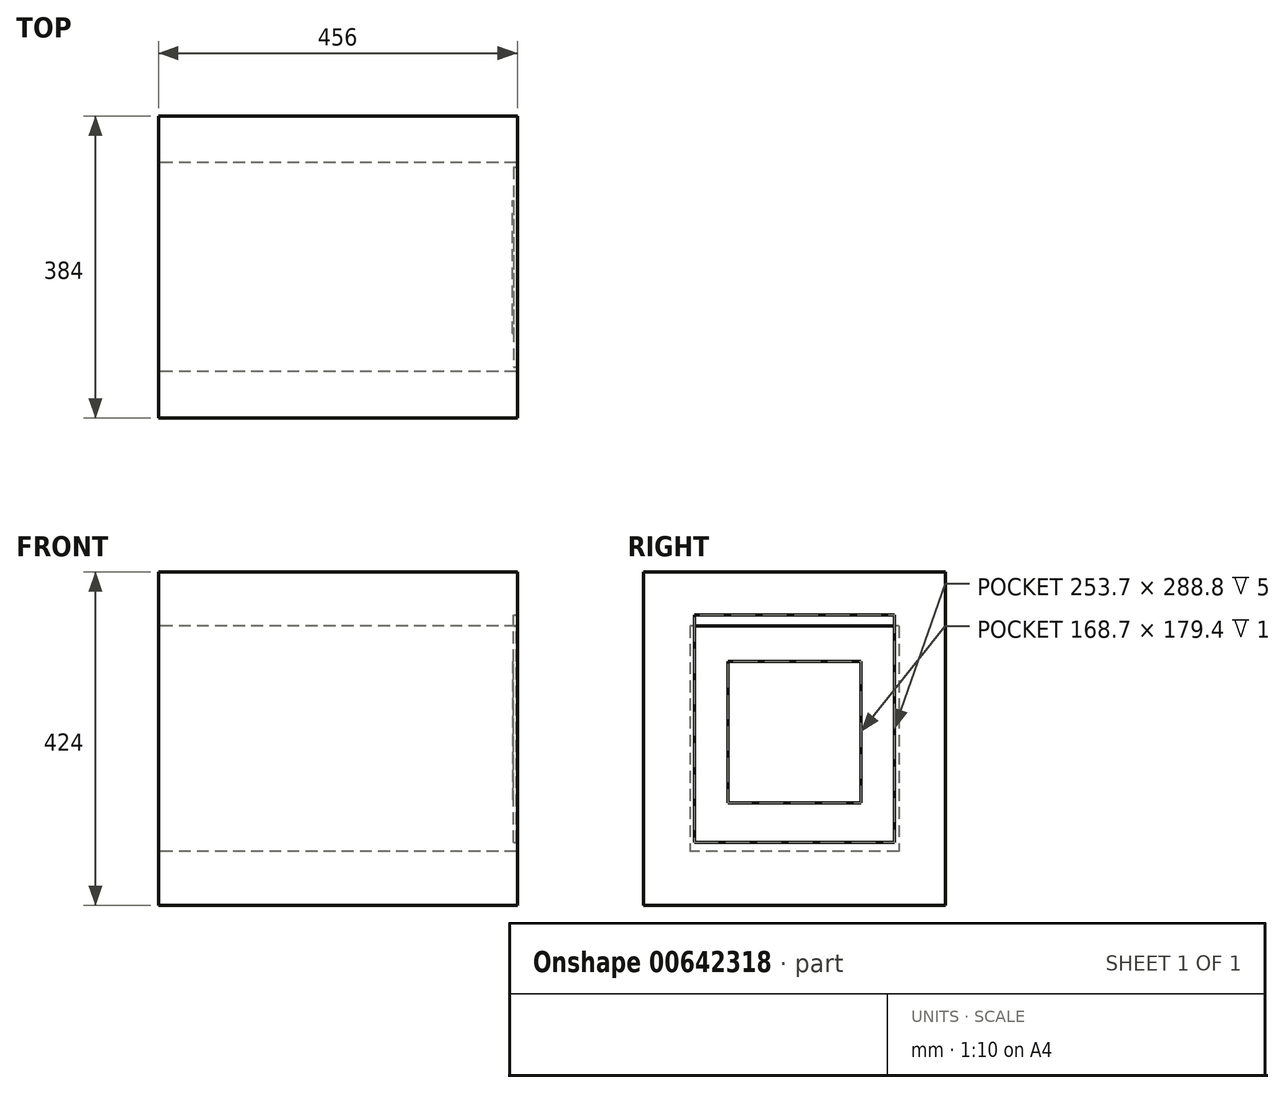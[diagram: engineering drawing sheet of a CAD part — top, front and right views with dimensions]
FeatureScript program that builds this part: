
annotation { "Feature Type Name" : "Feature", "Feature Type Description" : "" }
export const myFeature = defineFeature(function(context is Context, id is Id, definition is map)
    precondition{}
    {
        {
            var Q0;
            Q0=qCreatedBy(makeId("Right.planeOp"),FACE);
            var sketch = newSketch(context, id + "F0", { "sketchPlane" : qUnion([Q0])});
            skLineSegment(sketch, "E0.bottom", {"start": v(132.5, 143) * mm, "end": v(-132.5, 143) * mm});
            skLineSegment(sketch, "E0.top", {"start": v(132.5, -143) * mm, "end": v(-132.5, -143) * mm});
            skLineSegment(sketch, "E0.left", {"start": v(132.5, 143) * mm, "end": v(132.5, -143) * mm});
            skLineSegment(sketch, "E0.right", {"start": v(-132.5, 143) * mm, "end": v(-132.5, -143) * mm});
            skPoint(sketch, "E0.middle", {"position": v(0, 0) * mm});
            skSolve(sketch);
        }
        {
            var Q0;
            Q0=makeQuery(id+"F0.imprint","IMPRINT",FACE,{"disambiguationData":[TD([[makeQuery(id+"F0.imprint","IMPRINT",EDGE,{"derivedFrom":sQuery(id+"F0.wireOp",EDGE,"E0.bottom")}),1.0]])]});
            extrude(context, id + "F1", {"entities" : qUnion([Q0]), "depth" : 455 * mm, "offsetDistance" : 25 * mm});
        }
        {
            var Q0;
            Q0=makeQuery(id+"F1.opExtrude","CAP_FACE",FACE,{"disambiguationData":[OSD([sQuery(id+"F0.wireOp",EDGE,"E0.bottom"),sQuery(id+"F0.wireOp",EDGE,"E0.top"),sQuery(id+"F0.wireOp",EDGE,"E0.left"),sQuery(id+"F0.wireOp",EDGE,"E0.right")])],"isStart":false});
            var sketch = newSketch(context, id + "F2", { "sketchPlane" : qUnion([Q0])});
            skLineSegment(sketch, "E1.bottom", {"start": v(-84.35, 98) * mm, "end": v(84.35, 98) * mm});
            skLineSegment(sketch, "E1.top", {"start": v(-84.35, -81.4) * mm, "end": v(84.35, -81.4) * mm});
            skLineSegment(sketch, "E1.left", {"start": v(-84.35, 98) * mm, "end": v(-84.35, -81.4) * mm});
            skLineSegment(sketch, "E1.right", {"start": v(84.35, 98) * mm, "end": v(84.35, -81.4) * mm});
            skLineSegment(sketch, "E2", {"start": v(-84.35, 98) * mm, "end": v(-132.5, 98) * mm, "construction": true});
            skLineSegment(sketch, "E3", {"start": v(84.35, 98) * mm, "end": v(132.5, 98) * mm, "construction": true});
            skSolve(sketch);
        }
        {
            var Q0;
            Q0=makeQuery(id+"F2.imprint","IMPRINT",FACE,{"disambiguationData":[TD([[makeQuery(id+"F2.imprint","IMPRINT",EDGE,{"derivedFrom":sQuery(id+"F2.wireOp",EDGE,"E1.bottom")}),-1.0]])]});
            extrude(context, id + "F3", {"entities" : qUnion([Q0]), "operationType" : NewBodyOperationType.REMOVE, "oppositeDirection" : true, "depth" : 5 * mm, "offsetDistance" : 25 * mm});
        }
        {
            var Q0;
            Q0=qCreatedBy(makeId("Right.planeOp"),FACE);
            var sketch = newSketch(context, id + "F4", { "sketchPlane" : qUnion([Q0])});
            skLineSegment(sketch, "E4.bottom", {"start": v(192, -212) * mm, "end": v(-192, -212) * mm});
            skLineSegment(sketch, "E4.top", {"start": v(192, 212) * mm, "end": v(-192, 212) * mm});
            skLineSegment(sketch, "E4.left", {"start": v(192, -212) * mm, "end": v(192, 212) * mm});
            skLineSegment(sketch, "E4.right", {"start": v(-192, -212) * mm, "end": v(-192, 212) * mm});
            skPoint(sketch, "E4.middle", {"position": v(0, 0) * mm});
            skSolve(sketch);
        }
        {
            var Q0;
            Q0=makeQuery(id+"F4.imprint","IMPRINT",FACE,{"disambiguationData":[TD([[makeQuery(id+"F4.imprint","IMPRINT",EDGE,{"derivedFrom":sQuery(id+"F4.wireOp",EDGE,"E4.bottom")}),-1.0]])]});
            extrude(context, id + "F5", {"entities" : qUnion([Q0]), "depth" : 456 * mm, "offsetDistance" : 25 * mm});
        }
        {
            var Q0;
            Q0=makeQuery(id+"F5.opExtrude","CAP_FACE",FACE,{"disambiguationData":[OSD([sQuery(id+"F4.wireOp",EDGE,"E4.bottom"),sQuery(id+"F4.wireOp",EDGE,"E4.top"),sQuery(id+"F4.wireOp",EDGE,"E4.left"),sQuery(id+"F4.wireOp",EDGE,"E4.right")])],"isStart":false});
            var sketch = newSketch(context, id + "F6", { "sketchPlane" : qUnion([Q0])});
            skLineSegment(sketch, "E5.bottom", {"start": v(126.85, -131.8) * mm, "end": v(-126.85, -131.8) * mm});
            skLineSegment(sketch, "E5.top", {"start": v(126.85, 157) * mm, "end": v(-126.85, 157) * mm});
            skLineSegment(sketch, "E5.left", {"start": v(126.85, -131.8) * mm, "end": v(126.85, 157) * mm});
            skLineSegment(sketch, "E5.right", {"start": v(-126.85, -131.8) * mm, "end": v(-126.85, 157) * mm});
            skPoint(sketch, "E5.middle", {"position": v(0, 12.6) * mm});
            skLineSegment(sketch, "E6", {"start": v(-126.85, 157) * mm, "end": v(-192, 157) * mm, "construction": true});
            skLineSegment(sketch, "E7", {"start": v(126.85, 157) * mm, "end": v(192, 157) * mm, "construction": true});
            skSolve(sketch);
        }
        {
            var Q0;
            Q0=makeQuery(id+"F6.imprint","IMPRINT",FACE,{"disambiguationData":[TD([[makeQuery(id+"F6.imprint","IMPRINT",EDGE,{"derivedFrom":sQuery(id+"F6.wireOp",EDGE,"E5.bottom")}),-1.0]])]});
            extrude(context, id + "F7", {"entities" : qUnion([Q0]), "operationType" : NewBodyOperationType.REMOVE, "oppositeDirection" : true, "depth" : 5 * mm, "offsetDistance" : 25 * mm});
        }
    });
